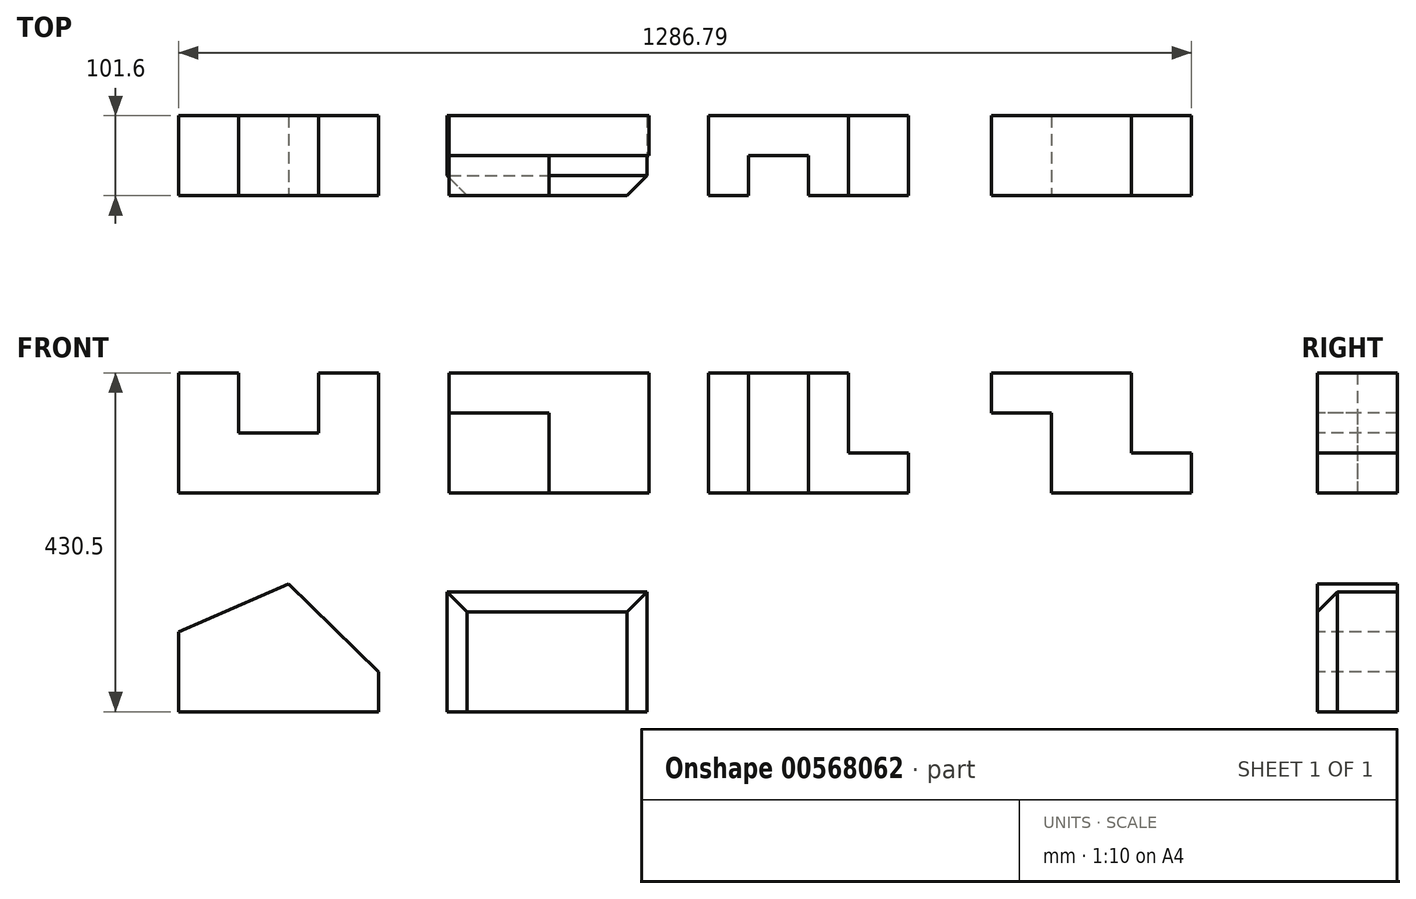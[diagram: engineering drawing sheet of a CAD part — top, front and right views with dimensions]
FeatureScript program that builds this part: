
annotation { "Feature Type Name" : "Feature", "Feature Type Description" : "" }
export const myFeature = defineFeature(function(context is Context, id is Id, definition is map)
    precondition{}
    {
        {
            var Q0;
            Q0=qCreatedBy(makeId("Front.planeOp"),FACE);
            var sketch = newSketch(context, id + "F0", { "sketchPlane" : qUnion([Q0])});
            skLineSegment(sketch, "E0", {"start": v(0, 0) * mm, "end": v(0, 152.4) * mm});
            skLineSegment(sketch, "E1", {"start": v(0, 0) * mm, "end": v(254, 0) * mm});
            skLineSegment(sketch, "E2", {"start": v(254, 0) * mm, "end": v(254, 152.4) * mm});
            skLineSegment(sketch, "E3", {"start": v(0, 152.4) * mm, "end": v(76.2, 152.4) * mm});
            skLineSegment(sketch, "E4", {"start": v(254, 152.4) * mm, "end": v(177.8, 152.4) * mm});
            skLineSegment(sketch, "E5", {"start": v(76.2, 152.4) * mm, "end": v(76.2, 76.2) * mm});
            skLineSegment(sketch, "E6", {"start": v(76.2, 76.2) * mm, "end": v(177.8, 76.2) * mm});
            skLineSegment(sketch, "E7", {"start": v(177.8, 76.2) * mm, "end": v(177.8, 152.4) * mm});
            skSolve(sketch);
        }
        {
            var Q0;
            Q0=makeQuery(id+"F0.imprint","IMPRINT",FACE,{"disambiguationData":[TD([[makeQuery(id+"F0.imprint","IMPRINT",EDGE,{"derivedFrom":sQuery(id+"F0.wireOp",EDGE,"E0")}),-1.0]])]});
            extrude(context, id + "F1", {"entities" : qUnion([Q0]), "oppositeDirection" : true, "depth" : 101.6 * mm, "offsetDistance" : 25.4 * mm});
        }
        {
            var Q0;
            Q0=qCreatedBy(makeId("Top.planeOp"),FACE);
            var sketch = newSketch(context, id + "F2", { "sketchPlane" : qUnion([Q0])});
            skLineSegment(sketch, "E8", {"start": v(343.48, 0) * mm, "end": v(343.48, 101.6) * mm});
            skLineSegment(sketch, "E9", {"start": v(343.48, 101.6) * mm, "end": v(597.48, 101.6) * mm});
            skLineSegment(sketch, "E10", {"start": v(597.48, 101.6) * mm, "end": v(597.48, 50.8) * mm});
            skLineSegment(sketch, "E11", {"start": v(597.48, 50.8) * mm, "end": v(597.48, 76.2) * mm});
            skLineSegment(sketch, "E12", {"start": v(597.48, 50.8) * mm, "end": v(470.48, 50.8) * mm});
            skLineSegment(sketch, "E13", {"start": v(470.48, 50.8) * mm, "end": v(470.48, 0) * mm});
            skLineSegment(sketch, "E14", {"start": v(470.48, 0) * mm, "end": v(343.48, 0) * mm});
            skSolve(sketch);
        }
        {
            var Q0;
            Q0=makeQuery(id+"F2.imprint","IMPRINT",FACE,{"disambiguationData":[TD([[makeQuery(id+"F2.imprint","IMPRINT",EDGE,{"derivedFrom":sQuery(id+"F2.wireOp",EDGE,"E8")}),-1.0]])]});
            extrude(context, id + "F3", {"entities" : qUnion([Q0]), "depth" : 152.4 * mm, "offsetDistance" : 25.4 * mm});
        }
        {
            var Q0;
            Q0=qCreatedBy(makeId("Top.planeOp"),FACE);
            var sketch = newSketch(context, id + "F4", { "sketchPlane" : qUnion([Q0])});
            skLineSegment(sketch, "E15", {"start": v(673.26, 0) * mm, "end": v(673.26, 101.6) * mm});
            skLineSegment(sketch, "E16", {"start": v(673.26, 101.6) * mm, "end": v(927.26, 101.6) * mm});
            skLineSegment(sketch, "E17", {"start": v(927.26, 101.6) * mm, "end": v(927.26, 0) * mm});
            skLineSegment(sketch, "E18", {"start": v(927.26, 0) * mm, "end": v(800.26, 0) * mm});
            skLineSegment(sketch, "E19", {"start": v(800.26, 0) * mm, "end": v(800.26, 50.8) * mm});
            skPoint(sketch, "E19.endSnap0", {"position": v(673.26, 50.8) * mm});
            skLineSegment(sketch, "E20", {"start": v(800.26, 50.8) * mm, "end": v(724.06, 50.8) * mm});
            skLineSegment(sketch, "E21", {"start": v(724.06, 50.8) * mm, "end": v(724.06, 0) * mm});
            skLineSegment(sketch, "E22", {"start": v(724.06, 0) * mm, "end": v(673.26, 0) * mm});
            skLineSegment(sketch, "E23", {"start": v(800.26, 0) * mm, "end": v(851.06, 0) * mm});
            skLineSegment(sketch, "E24", {"start": v(851.06, 0) * mm, "end": v(851.06, 101.6) * mm});
            skSolve(sketch);
        }
        {
            var Q0;
            Q0=makeQuery(id+"F4.imprint","IMPRINT",FACE,{"disambiguationData":[TD([[makeQuery(id+"F4.imprint","IMPRINT",EDGE,{"derivedFrom":sQuery(id+"F4.wireOp",EDGE,"E15")}),-1.0]])]});
            extrude(context, id + "F5", {"entities" : qUnion([Q0]), "depth" : 152.4 * mm, "offsetDistance" : 25.4 * mm});
        }
        {
            var Q0;
            {var subQ0=sQuery(id+"F4.wireOp",EDGE,"E17");Q0=makeQuery(id+"F4.imprint","IMPRINT",FACE,{"disambiguationData":[TD([[makeQuery(id+"F4.imprint","IMPRINT",EDGE,{"derivedFrom":subQ0}),-1.0]])]});}
            extrude(context, id + "F6", {"entities" : qUnion([Q0]), "operationType" : NewBodyOperationType.ADD, "depth" : 50.8 * mm, "offsetDistance" : 25.4 * mm});
        }
        {
            var Q0;
            {var subQ0=sQuery(id+"F2.wireOp",EDGE,"E9");Q0=makeQuery(id+"F2.imprint","IMPRINT",FACE,{"disambiguationData":[TD([[makeQuery(id+"F2.imprint","IMPRINT",EDGE,{"derivedFrom":subQ0}),-1.0]])]});}
            extrude(context, id + "F7", {"entities" : qUnion([Q0]), "operationType" : NewBodyOperationType.ADD, "depth" : 152.4 * mm, "offsetDistance" : 25.4 * mm});
        }
        {
            var Q0;
            Q0=makeQuery(id+"F3.opExtrude","SWEPT_FACE",FACE,{"disambiguationData":[OSD([sQuery(id+"F2.wireOp",EDGE,"E14")])]});
            var sketch = newSketch(context, id + "F8", { "sketchPlane" : qUnion([Q0])});
            skSolve(sketch);
        }
        {
            var Q0;
            {var subQ0=sQuery(id+"F2.wireOp",EDGE,"E14");Q0=makeQuery(id+"F8.imprint","IMPRINT",FACE,{"disambiguationData":[TD([[makeQuery(id+"F8.imprint","IMPRINT",EDGE,{"derivedFrom":makeQuery(id+"F3.opExtrude","CAP_EDGE",EDGE,{"disambiguationData":[OSD([subQ0])],"isStart":true})}),-1.0]])]});}
            var sketch = newSketch(context, id + "F9", { "sketchPlane" : qUnion([Q0])});
            skLineSegment(sketch, "E25.bottom", {"start": v(343.48, 152.4) * mm, "end": v(470.48, 152.4) * mm});
            skLineSegment(sketch, "E25.top", {"start": v(343.48, 101.6) * mm, "end": v(470.48, 101.6) * mm});
            skLineSegment(sketch, "E25.left", {"start": v(343.48, 152.4) * mm, "end": v(343.48, 101.6) * mm});
            skLineSegment(sketch, "E25.right", {"start": v(470.48, 152.4) * mm, "end": v(470.48, 101.6) * mm});
            skSolve(sketch);
        }
        {
            var Q0;
            Q0=makeQuery(id+"F9.imprint","IMPRINT",FACE,{"disambiguationData":[TD([[makeQuery(id+"F9.imprint","IMPRINT",EDGE,{"derivedFrom":sQuery(id+"F9.wireOp",EDGE,"E25.bottom")}),1.0]])]});
            extrude(context, id + "F10", {"entities" : qUnion([Q0]), "operationType" : NewBodyOperationType.REMOVE, "oppositeDirection" : true, "depth" : 50.8 * mm, "offsetDistance" : 25.4 * mm});
        }
        {
            var Q0;
            Q0=makeQuery(id+"F6.boolean.opBoolean","MERGE",FACE,{"derivedFrom":[makeQuery(id+"F5.opExtrude","SWEPT_FACE",FACE,{"disambiguationData":[OSD([sQuery(id+"F4.wireOp",EDGE,"E23")])]}),makeQuery(id+"F6.opExtrude","SWEPT_FACE",FACE,{"disambiguationData":[OSD([sQuery(id+"F4.wireOp",EDGE,"E18")])]})]});
            var sketch = newSketch(context, id + "F11", { "sketchPlane" : qUnion([Q0])});
            skLineSegment(sketch, "E26", {"start": v(1032.79, 101.6) * mm, "end": v(1032.79, 152.4) * mm});
            skPoint(sketch, "E26.startSnap0", {"position": v(851.06, 101.6) * mm});
            skLineSegment(sketch, "E27", {"start": v(1032.79, 152.4) * mm, "end": v(1210.59, 152.4) * mm});
            skLineSegment(sketch, "E28", {"start": v(1210.59, 152.4) * mm, "end": v(1210.59, 50.8) * mm});
            skLineSegment(sketch, "E29", {"start": v(1210.59, 50.8) * mm, "end": v(1286.79, 50.8) * mm});
            skLineSegment(sketch, "E30", {"start": v(1286.79, 50.8) * mm, "end": v(1286.79, 0) * mm});
            skLineSegment(sketch, "E31", {"start": v(1286.79, 0) * mm, "end": v(1108.99, 0) * mm});
            skPoint(sketch, "E31.endSnap0", {"position": v(1121.69, 152.4) * mm});
            skLineSegment(sketch, "E32", {"start": v(1032.79, 101.6) * mm, "end": v(1108.99, 101.6) * mm});
            skLineSegment(sketch, "E33", {"start": v(1108.99, 101.6) * mm, "end": v(1108.99, 0) * mm});
            skSolve(sketch);
        }
        {
            var Q0;
            Q0=makeQuery(id+"F11.imprint","IMPRINT",FACE,{"disambiguationData":[TD([[makeQuery(id+"F11.imprint","IMPRINT",EDGE,{"derivedFrom":sQuery(id+"F11.wireOp",EDGE,"E26")}),-1.0]])]});
            extrude(context, id + "F12", {"entities" : qUnion([Q0]), "oppositeDirection" : true, "depth" : 101.6 * mm, "offsetDistance" : 25.4 * mm});
        }
        {
            var Q0;
            Q0=qCreatedBy(makeId("Front.planeOp"),FACE);
            var sketch = newSketch(context, id + "F13", { "sketchPlane" : qUnion([Q0])});
            skLineSegment(sketch, "E34", {"start": v(0, -278.1) * mm, "end": v(254, -278.1) * mm});
            skLineSegment(sketch, "E35", {"start": v(254, -278.1) * mm, "end": v(254, -227.3) * mm});
            skLineSegment(sketch, "E36", {"start": v(0, -278.1) * mm, "end": v(0, -176.5) * mm});
            skLineSegment(sketch, "E37", {"start": v(0, -176.5) * mm, "end": v(139.65, -115.47) * mm});
            skLineSegment(sketch, "E38", {"start": v(139.65, -115.47) * mm, "end": v(254, -227.3) * mm});
            skSolve(sketch);
        }
        {
            var Q0;
            Q0=makeQuery(id+"F13.imprint","IMPRINT",FACE,{"disambiguationData":[TD([[makeQuery(id+"F13.imprint","IMPRINT",EDGE,{"derivedFrom":sQuery(id+"F13.wireOp",EDGE,"E34")}),1.0]])]});
            extrude(context, id + "F14", {"entities" : qUnion([Q0]), "oppositeDirection" : true, "depth" : 101.6 * mm, "offsetDistance" : 25.4 * mm});
        }
        {
            var Q0;
            Q0=makeQuery(id+"F14.opExtrude","CAP_FACE",FACE,{"disambiguationData":[OSD([sQuery(id+"F13.wireOp",EDGE,"E34"),sQuery(id+"F13.wireOp",EDGE,"E35"),sQuery(id+"F13.wireOp",EDGE,"E36"),sQuery(id+"F13.wireOp",EDGE,"E37"),sQuery(id+"F13.wireOp",EDGE,"E38")])],"isStart":true});
            var sketch = newSketch(context, id + "F15", { "sketchPlane" : qUnion([Q0])});
            skLineSegment(sketch, "E39", {"start": v(341.12, -278.1) * mm, "end": v(341.12, -125.7) * mm});
            skLineSegment(sketch, "E40", {"start": v(341.12, -278.1) * mm, "end": v(595.12, -278.1) * mm});
            skLineSegment(sketch, "E41", {"start": v(595.12, -278.1) * mm, "end": v(595.12, -125.7) * mm});
            skLineSegment(sketch, "E42", {"start": v(595.12, -125.7) * mm, "end": v(341.12, -125.7) * mm});
            skLineSegment(sketch, "E43", {"start": v(364.2, -251.36) * mm, "end": v(364.2, -149.76) * mm});
            skLineSegment(sketch, "E44", {"start": v(364.2, -251.36) * mm, "end": v(567.4, -251.36) * mm});
            skLineSegment(sketch, "E45", {"start": v(567.4, -251.36) * mm, "end": v(567.4, -149.76) * mm});
            skLineSegment(sketch, "E46", {"start": v(567.4, -149.76) * mm, "end": v(364.2, -149.76) * mm});
            skSolve(sketch);
        }
        {
            var Q0;
            Q0=makeQuery(id+"F15.imprint","IMPRINT",FACE,{"disambiguationData":[TD([[makeQuery(id+"F15.imprint","IMPRINT",EDGE,{"derivedFrom":sQuery(id+"F15.wireOp",EDGE,"E39")}),-1.0]])]});
            extrude(context, id + "F16", {"entities" : qUnion([Q0]), "oppositeDirection" : true, "depth" : 101.6 * mm, "offsetDistance" : 25.4 * mm});
        }
        {
            var Q0;
            Q0=makeQuery(id+"F16.opExtrude","SWEPT_FACE",FACE,{"disambiguationData":[OSD([sQuery(id+"F15.wireOp",EDGE,"E44")])]});
            extrude(context, id + "F17", {"entities" : qUnion([Q0]), "operationType" : NewBodyOperationType.ADD, "depth" : 109.22 * mm, "offsetDistance" : 25.4 * mm});
        }
        {
            var Q0;
            Q0=makeQuery(id+"F16.opExtrude","CAP_EDGE",EDGE,{"disambiguationData":[OSD([sQuery(id+"F15.wireOp",EDGE,"E42")])],"isStart":true});
            var Q1;
            Q1=makeQuery(id+"F16.opExtrude","CAP_EDGE",EDGE,{"disambiguationData":[OSD([sQuery(id+"F15.wireOp",EDGE,"E41")])],"isStart":true});
            var Q2;
            Q2=makeQuery(id+"F16.opExtrude","CAP_EDGE",EDGE,{"disambiguationData":[OSD([sQuery(id+"F15.wireOp",EDGE,"E39")])],"isStart":true});
            chamfer(context, id + "F18", {"entities" : qUnion([Q0, Q1, Q2]), "width" : 25.4 * mm, "tangentPropagation" : true});
        }
    });
